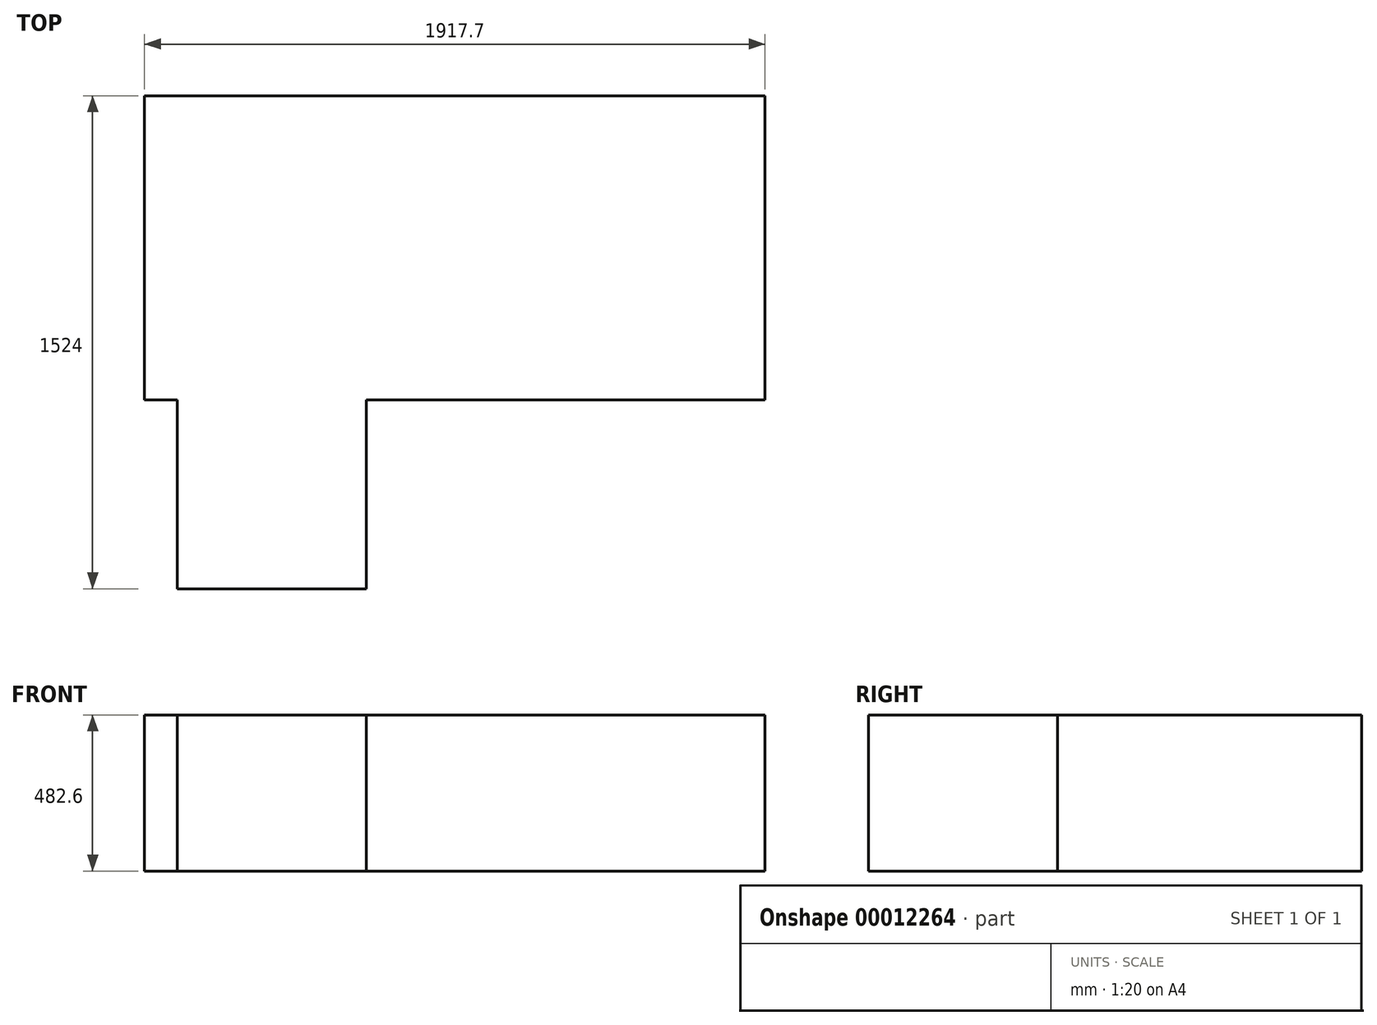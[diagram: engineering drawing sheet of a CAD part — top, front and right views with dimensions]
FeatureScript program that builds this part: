
annotation { "Feature Type Name" : "Feature", "Feature Type Description" : "" }
export const myFeature = defineFeature(function(context is Context, id is Id, definition is map)
    precondition{}
    {
        {
            var Q0;
            Q0=qCreatedBy(makeId("Top.planeOp"),FACE);
            cPlane(context, id + "F0", {"entities" : qUnion([Q0]), "cplaneType" : CPlaneType.OFFSET, "offset" : 63.5 * mm, "width" : 152.4 * mm, "height" : 152.4 * mm});
        }
        {
            var Q0;
            Q0=qCreatedBy(id+"F0.planeOp",FACE);
            var sketch = newSketch(context, id + "F1", { "sketchPlane" : qUnion([Q0])});
            skLineSegment(sketch, "E0", {"start": v(0, 0) * mm, "end": v(958.85, 0) * mm});
            skLineSegment(sketch, "E1", {"start": v(958.85, 0) * mm, "end": v(958.85, -939.8) * mm});
            skLineSegment(sketch, "E2", {"start": v(958.85, -939.8) * mm, "end": v(0, -939.8) * mm});
            skLineSegment(sketch, "E3", {"start": v(0, -939.8) * mm, "end": v(0, 0) * mm});
            skLineSegment(sketch, "E4", {"start": v(0, 0) * mm, "end": v(0, 305.25) * mm, "construction": true});
            skLineSegment(sketch, "E5", {"start": v(857.25, -939.8) * mm, "end": v(857.25, 0) * mm});
            skLineSegment(sketch, "E6", {"start": v(0, -254) * mm, "end": v(857.25, -254) * mm});
            skSolve(sketch);
        }
        {
            var Q0;
            Q0=qCreatedBy(makeId("Top.planeOp"),FACE);
            var sketch = newSketch(context, id + "F2", { "sketchPlane" : qUnion([Q0])});
            skLineSegment(sketch, "E7", {"start": v(-958.85, 0) * mm, "end": v(958.85, 0) * mm});
            skLineSegment(sketch, "E8", {"start": v(958.85, 0) * mm, "end": v(958.85, -939.8) * mm});
            skLineSegment(sketch, "E9", {"start": v(958.85, -939.8) * mm, "end": v(-273.05, -939.8) * mm});
            skLineSegment(sketch, "E10", {"start": v(-273.05, -939.8) * mm, "end": v(-273.05, -1524) * mm});
            skLineSegment(sketch, "E11", {"start": v(-273.05, -1524) * mm, "end": v(-857.25, -1524) * mm});
            skLineSegment(sketch, "E12", {"start": v(-857.25, -1524) * mm, "end": v(-857.25, -939.8) * mm});
            skLineSegment(sketch, "E13", {"start": v(-857.25, -939.8) * mm, "end": v(-958.85, -939.8) * mm});
            skLineSegment(sketch, "E14", {"start": v(-958.85, -939.8) * mm, "end": v(-958.85, 0) * mm});
            skSolve(sketch);
        }
        {
            var Q0;
            Q0 = qSketchRegion(id + "F2", true);
            extrude(context, id + "F3", {"entities" : qUnion([Q0]), "depth" : 482.6 * mm});
        }
    });
